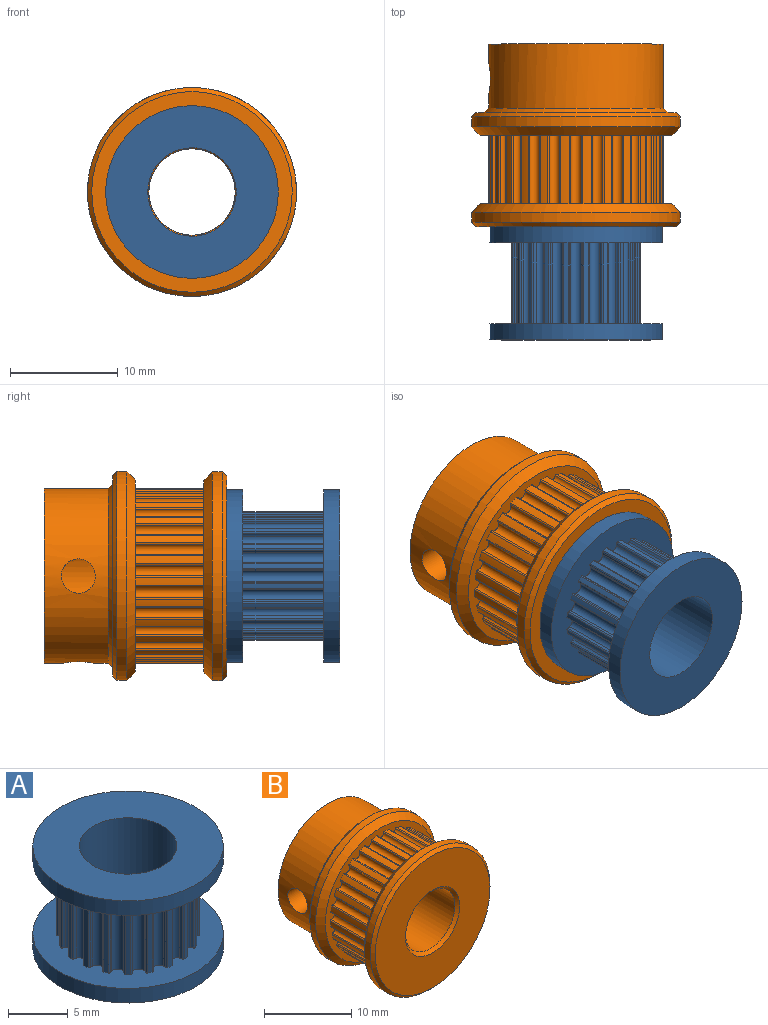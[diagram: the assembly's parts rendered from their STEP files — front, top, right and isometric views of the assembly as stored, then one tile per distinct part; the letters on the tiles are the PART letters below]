
ASSEMBLY  parts=2 mates=1
PART A: 127 faces, bbox 16x16x10.5 mm
  f0: cylinder r=1mm len=7.5mm, axis (0,0,-1), area 1.9mm2, adj f1,f119,f120,f123
  f1: cylinder r=0.15mm len=7.5mm, axis (0,0,-1), area 1.4mm2, adj f0,f2,f120,f123
  f2: cylinder r=6mm len=7.5mm, axis (0,0,-1), area 3.3mm2, adj f1,f3,f120,f123
  f3: cylinder r=0.15mm len=7.5mm, axis (0,0,-1), area 1.4mm2, adj f2,f4,f120,f123
  f4: cylinder r=1mm len=7.5mm, axis (0,0,-1), area 1.9mm2, adj f3,f5,f120,f123
  f5: cylinder r=0.56mm len=7.5mm, axis (0,0,-1), area 9.8mm2, adj f4,f6,f120,f123
  f6: cylinder r=1mm len=7.5mm, axis (0,0,-1), area 1.9mm2, adj f5,f7,f120,f123
  f7: cylinder r=0.15mm len=7.5mm, axis (0,0,-1), area 1.4mm2, adj f6,f8,f120,f123
  f8: cylinder r=6mm len=7.5mm, axis (0,0,-1), area 3.3mm2, adj f7,f9,f120,f123
  f9: cylinder r=0.15mm len=7.5mm, axis (0,0,-1), area 1.4mm2, adj f8,f10,f120,f123
  f10: cylinder r=1mm len=7.5mm, axis (0,0,-1), area 1.9mm2, adj f9,f11,f120,f123
  f11: cylinder r=0.56mm len=7.5mm, axis (0,0,-1), area 9.8mm2, adj f10,f12,f120,f123
  f12: cylinder r=1mm len=7.5mm, axis (0,0,-1), area 1.9mm2, adj f11,f13,f120,f123
  f13: cylinder r=0.15mm len=7.5mm, axis (0,0,-1), area 1.4mm2, adj f12,f14,f120,f123
  f14: cylinder r=6mm len=7.5mm, axis (0,0,-1), area 3.3mm2, adj f13,f15,f120,f123
  f15: cylinder r=0.15mm len=7.5mm, axis (0,0,-1), area 1.4mm2, adj f14,f16,f120,f123
  f16: cylinder r=1mm len=7.5mm, axis (0,0,-1), area 1.9mm2, adj f15,f17,f120,f123
  f17: cylinder r=0.56mm len=7.5mm, axis (0,0,-1), area 9.8mm2, adj f16,f18,f120,f123
  f18: cylinder r=1mm len=7.5mm, axis (0,0,-1), area 1.9mm2, adj f17,f19,f120,f123
  f19: cylinder r=0.15mm len=7.5mm, axis (0,0,-1), area 1.4mm2, adj f18,f20,f120,f123
  f20: cylinder r=6mm len=7.5mm, axis (0,0,-1), area 3.3mm2, adj f19,f21,f120,f123
  f21: cylinder r=0.15mm len=7.5mm, axis (0,0,-1), area 1.4mm2, adj f20,f22,f120,f123
  f22: cylinder r=1mm len=7.5mm, axis (0,0,-1), area 1.9mm2, adj f21,f23,f120,f123
  f23: cylinder r=0.56mm len=7.5mm, axis (0,0,-1), area 9.8mm2, adj f22,f24,f120,f123
  f24: cylinder r=1mm len=7.5mm, axis (0,0,-1), area 1.9mm2, adj f23,f25,f120,f123
  f25: cylinder r=0.15mm len=7.5mm, axis (0,0,-1), area 1.4mm2, adj f24,f26,f120,f123
  f26: cylinder r=6mm len=7.5mm, axis (0,0,-1), area 2.8mm2, adj f25,f27,f120,f123
  f27: cylinder r=0.15mm len=7.5mm, axis (0,0,-1), area 2mm2, adj f26,f28,f120,f123
  f28: cylinder r=1mm len=7.5mm, axis (0,0,-1), area 1.9mm2, adj f27,f29,f120,f123
  f29: cylinder r=0.56mm len=7.5mm, axis (0,0,-1), area 9.8mm2, adj f28,f30,f120,f123
  f30: cylinder r=1mm len=7.5mm, axis (0,0,-1), area 1.9mm2, adj f29,f31,f120,f123
  f31: cylinder r=0.15mm len=7.5mm, axis (0,0,-1), area 1.4mm2, adj f30,f32,f120,f123
  f32: cylinder r=6mm len=7.5mm, axis (0,0,-1), area 3.3mm2, adj f31,f33,f120,f123
  f33: cylinder r=0.15mm len=7.5mm, axis (0,0,-1), area 1.4mm2, adj f32,f34,f120,f123
  f34: cylinder r=1mm len=7.5mm, axis (0,0,-1), area 1.9mm2, adj f33,f35,f120,f123
  f35: cylinder r=0.56mm len=7.5mm, axis (0,0,-1), area 9.8mm2, adj f34,f36,f120,f123
  f36: cylinder r=1mm len=7.5mm, axis (0,0,-1), area 1.9mm2, adj f35,f37,f120,f123
  f37: cylinder r=0.15mm len=7.5mm, axis (0,0,-1), area 1.4mm2, adj f36,f38,f120,f123
  f38: cylinder r=6mm len=7.5mm, axis (0,0,-1), area 3.3mm2, adj f37,f39,f120,f123
  f39: cylinder r=0.15mm len=7.5mm, axis (0,0,-1), area 1.4mm2, adj f38,f40,f120,f123
  f40: cylinder r=1mm len=7.5mm, axis (0,0,-1), area 1.9mm2, adj f39,f41,f120,f123
  f41: cylinder r=0.56mm len=7.5mm, axis (0,0,-1), area 9.8mm2, adj f40,f42,f120,f123
  f42: cylinder r=1mm len=7.5mm, axis (0,0,-1), area 1.9mm2, adj f41,f43,f120,f123
  f43: cylinder r=0.15mm len=7.5mm, axis (0,0,-1), area 1.4mm2, adj f42,f44,f120,f123
  f44: cylinder r=6mm len=7.5mm, axis (0,0,-1), area 3.3mm2, adj f43,f45,f120,f123
  f45: cylinder r=0.15mm len=7.5mm, axis (0,0,-1), area 1.4mm2, adj f44,f46,f120,f123
  f46: cylinder r=1mm len=7.5mm, axis (0,0,-1), area 1.9mm2, adj f45,f47,f120,f123
  f47: cylinder r=0.56mm len=7.5mm, axis (0,0,-1), area 9.8mm2, adj f46,f48,f120,f123
  f48: cylinder r=1mm len=7.5mm, axis (0,0,-1), area 1.9mm2, adj f47,f49,f120,f123
  f49: cylinder r=0.15mm len=7.5mm, axis (0,0,-1), area 1.4mm2, adj f48,f50,f120,f123
  f50: cylinder r=6mm len=7.5mm, axis (0,0,-1), area 3.3mm2, adj f49,f51,f120,f123
  f51: cylinder r=0.15mm len=7.5mm, axis (0,0,-1), area 1.4mm2, adj f50,f52,f120,f123
  f52: cylinder r=1mm len=7.5mm, axis (0,0,-1), area 1.9mm2, adj f51,f53,f120,f123
  f53: cylinder r=0.56mm len=7.5mm, axis (0,0,-1), area 9.8mm2, adj f52,f54,f120,f123
  f54: cylinder r=1mm len=7.5mm, axis (0,0,-1), area 1.9mm2, adj f53,f55,f120,f123
  f55: cylinder r=0.15mm len=7.5mm, axis (0,0,-1), area 1.4mm2, adj f54,f56,f120,f123
  f56: cylinder r=6mm len=7.5mm, axis (0,0,-1), area 3.3mm2, adj f55,f57,f120,f123
  f57: cylinder r=0.15mm len=7.5mm, axis (0,0,-1), area 1.4mm2, adj f56,f58,f120,f123
  f58: cylinder r=1mm len=7.5mm, axis (0,0,-1), area 1.9mm2, adj f57,f59,f120,f123
  f59: cylinder r=0.56mm len=7.5mm, axis (0,0,-1), area 9.8mm2, adj f58,f60,f120,f123
  f60: cylinder r=1mm len=7.5mm, axis (0,0,-1), area 1.9mm2, adj f59,f61,f120,f123
  f61: cylinder r=0.15mm len=7.5mm, axis (0,0,-1), area 1.4mm2, adj f60,f62,f120,f123
  f62: cylinder r=6mm len=7.5mm, axis (0,0,-1), area 3.3mm2, adj f61,f63,f120,f123
  f63: cylinder r=0.15mm len=7.5mm, axis (0,0,-1), area 1.4mm2, adj f62,f64,f120,f123
  f64: cylinder r=1mm len=7.5mm, axis (0,0,-1), area 1.9mm2, adj f63,f65,f120,f123
  f65: cylinder r=0.56mm len=7.5mm, axis (0,0,-1), area 9.8mm2, adj f64,f66,f120,f123
  f66: cylinder r=1mm len=7.5mm, axis (0,0,-1), area 1.9mm2, adj f65,f67,f120,f123
  f67: cylinder r=0.15mm len=7.5mm, axis (0,0,-1), area 1.4mm2, adj f66,f68,f120,f123
  f68: cylinder r=6mm len=7.5mm, axis (0,0,-1), area 3.3mm2, adj f67,f69,f120,f123
  f69: cylinder r=0.15mm len=7.5mm, axis (0,0,-1), area 1.4mm2, adj f68,f70,f120,f123
  f70: cylinder r=1mm len=7.5mm, axis (0,0,-1), area 1.9mm2, adj f69,f71,f120,f123
  f71: cylinder r=0.56mm len=7.5mm, axis (0,0,-1), area 9.8mm2, adj f70,f72,f120,f123
  f72: cylinder r=1mm len=7.5mm, axis (0,0,-1), area 1.9mm2, adj f71,f73,f120,f123
  f73: cylinder r=0.15mm len=7.5mm, axis (0,0,-1), area 1.4mm2, adj f72,f74,f120,f123
  f74: cylinder r=6mm len=7.5mm, axis (0,0,-1), area 3.3mm2, adj f73,f75,f120,f123
  f75: cylinder r=0.15mm len=7.5mm, axis (0,0,-1), area 1.4mm2, adj f74,f76,f120,f123
  f76: cylinder r=1mm len=7.5mm, axis (0,0,-1), area 1.9mm2, adj f75,f77,f120,f123
  f77: cylinder r=0.56mm len=7.5mm, axis (0,0,-1), area 9.8mm2, adj f76,f78,f120,f123
  f78: cylinder r=1mm len=7.5mm, axis (0,0,-1), area 1.9mm2, adj f77,f79,f120,f123
  f79: cylinder r=0.15mm len=7.5mm, axis (0,0,-1), area 1.4mm2, adj f78,f80,f120,f123
  f80: cylinder r=6mm len=7.5mm, axis (0,0,-1), area 3.3mm2, adj f79,f81,f120,f123
  f81: cylinder r=0.15mm len=7.5mm, axis (0,0,-1), area 1.4mm2, adj f80,f82,f120,f123
  f82: cylinder r=1mm len=7.5mm, axis (0,0,-1), area 1.9mm2, adj f81,f83,f120,f123
  f83: cylinder r=0.56mm len=7.5mm, axis (0,0,-1), area 9.8mm2, adj f82,f84,f120,f123
  f84: cylinder r=1mm len=7.5mm, axis (0,0,-1), area 1.9mm2, adj f83,f85,f120,f123
  f85: cylinder r=0.15mm len=7.5mm, axis (0,0,-1), area 1.4mm2, adj f84,f86,f120,f123
  f86: cylinder r=6mm len=7.5mm, axis (0,0,-1), area 3.3mm2, adj f85,f87,f120,f123
  f87: cylinder r=0.15mm len=7.5mm, axis (0,0,-1), area 1.4mm2, adj f86,f88,f120,f123
  f88: cylinder r=1mm len=7.5mm, axis (0,0,-1), area 1.9mm2, adj f87,f89,f120,f123
  f89: cylinder r=0.56mm len=7.5mm, axis (0,0,-1), area 9.8mm2, adj f88,f90,f120,f123
  f90: cylinder r=1mm len=7.5mm, axis (0,0,-1), area 1.9mm2, adj f89,f91,f120,f123
  f91: cylinder r=0.15mm len=7.5mm, axis (0,0,-1), area 1.4mm2, adj f90,f92,f120,f123
  f92: cylinder r=6mm len=7.5mm, axis (0,0,-1), area 3.3mm2, adj f91,f93,f120,f123
  f93: cylinder r=0.15mm len=7.5mm, axis (0,0,-1), area 1.4mm2, adj f92,f94,f120,f123
  f94: cylinder r=1mm len=7.5mm, axis (0,0,-1), area 1.9mm2, adj f93,f95,f120,f123
  f95: cylinder r=0.56mm len=7.5mm, axis (0,0,-1), area 9.8mm2, adj f94,f96,f120,f123
  f96: cylinder r=1mm len=7.5mm, axis (0,0,-1), area 1.9mm2, adj f95,f97,f120,f123
  f97: cylinder r=0.15mm len=7.5mm, axis (0,0,-1), area 1.4mm2, adj f96,f98,f120,f123
  f98: cylinder r=6mm len=7.5mm, axis (0,0,-1), area 3.3mm2, adj f97,f99,f120,f123
  f99: cylinder r=0.15mm len=7.5mm, axis (0,0,-1), area 1.4mm2, adj f98,f100,f120,f123
  f100: cylinder r=1mm len=7.5mm, axis (0,0,-1), area 1.9mm2, adj f99,f101,f120,f123
  f101: cylinder r=0.56mm len=7.5mm, axis (0,0,-1), area 9.8mm2, adj f100,f102,f120,f123
  f102: cylinder r=1mm len=7.5mm, axis (0,0,-1), area 1.9mm2, adj f101,f103,f120,f123
  f103: cylinder r=0.15mm len=7.5mm, axis (0,0,-1), area 1.4mm2, adj f102,f104,f120,f123
  f104: cylinder r=6mm len=7.5mm, axis (0,0,-1), area 3.3mm2, adj f103,f105,f120,f123
  f105: cylinder r=0.15mm len=7.5mm, axis (0,0,-1), area 1.4mm2, adj f104,f106,f120,f123
  f106: cylinder r=1mm len=7.5mm, axis (0,0,-1), area 1.9mm2, adj f105,f107,f120,f123
  f107: cylinder r=0.56mm len=7.5mm, axis (0,0,-1), area 9.8mm2, adj f106,f108,f120,f123
  f108: cylinder r=1mm len=7.5mm, axis (0,0,-1), area 1.9mm2, adj f107,f109,f120,f123
  f109: cylinder r=0.15mm len=7.5mm, axis (0,0,-1), area 1.4mm2, adj f108,f110,f120,f123
  f110: cylinder r=6mm len=7.5mm, axis (0,0,-1), area 3.3mm2, adj f109,f111,f120,f123
  f111: cylinder r=0.15mm len=7.5mm, axis (0,0,-1), area 1.4mm2, adj f110,f112,f120,f123
  f112: cylinder r=1mm len=7.5mm, axis (0,0,-1), area 1.9mm2, adj f111,f113,f120,f123
  f113: cylinder r=0.56mm len=7.5mm, axis (0,0,-1), area 9.8mm2, adj f112,f114,f120,f123
  f114: cylinder r=1mm len=7.5mm, axis (0,0,-1), area 1.9mm2, adj f113,f115,f120,f123
  f115: cylinder r=0.15mm len=7.5mm, axis (0,0,-1), area 1.4mm2, adj f114,f116,f120,f123
  f116: cylinder r=6mm len=7.5mm, axis (0,0,-1), area 3.3mm2, adj f115,f117,f120,f123
  f117: cylinder r=0.15mm len=7.5mm, axis (0,0,-1), area 1.4mm2, adj f116,f118,f120,f123
  f118: cylinder r=1mm len=7.5mm, axis (0,0,-1), area 1.9mm2, adj f117,f119,f120,f123
  f119: cylinder r=0.56mm len=7.5mm, axis (0,0,-1), area 9.8mm2, adj f0,f118,f120,f123
  f120: plane 16x16mm, normal (0,0,-1), area 102.3mm2, adj f0,f1,f2,f3,f4,f5,f6,f7
  f121: cylinder r=8mm len=16mm, axis (0,0,-1), area 75.4mm2, adj f120,f122
  f122: plane 16x16mm, normal (0,0,1), area 148.3mm2, adj f121,f126
  f123: plane 16x16mm, normal (0,0,1), area 102.3mm2, adj f0,f1,f2,f3,f4,f5,f6,f7
  f124: cylinder r=8mm len=16mm, axis (0,0,1), area 75.4mm2, adj f123,f125
  f125: plane 16x16mm, normal (0,0,-1), area 148.3mm2, adj f124,f126
  f126: cylinder r=4.1mm len=10.5mm, axis (0,0,-1), area 270.5mm2, adj f122,f125
PART B: 117 faces, bbox 19.4x16.9x19.4 mm
  f0: cylinder r=8.1mm len=16.21mm, axis (0,-1,0), area 287.2mm2, adj f1,f108,f114,f116
  f1: cylinder r=1.59mm len=4.43mm, axis (1,0,0), area 41.8mm2, adj f0,f109
  f2: cylinder r=0.5mm len=6.35mm, axis (0,1,0), area 9.8mm2, adj f3,f101,f102,f105
  f3: cylinder r=0.12mm len=6.35mm, axis (0,1,0), area 1.3mm2, adj f2,f4,f102,f105
  f4: cylinder r=8.1mm len=6.35mm, axis (0,1,0), area 4.9mm2, adj f3,f5,f102,f105
  f5: cylinder r=0.12mm len=6.35mm, axis (0,1,0), area 1.3mm2, adj f4,f6,f102,f105
  f6: cylinder r=0.5mm len=6.35mm, axis (0,1,0), area 9.8mm2, adj f5,f7,f102,f105
  f7: cylinder r=0.12mm len=6.35mm, axis (0,1,0), area 1.3mm2, adj f6,f8,f102,f105
  f8: cylinder r=8.1mm len=6.35mm, axis (0,1,0), area 4.9mm2, adj f7,f9,f102,f105
  f9: cylinder r=0.12mm len=6.35mm, axis (0,1,0), area 1.3mm2, adj f8,f10,f102,f105
  f10: cylinder r=0.5mm len=6.35mm, axis (0,1,0), area 9.8mm2, adj f9,f11,f102,f105
  f11: cylinder r=0.12mm len=6.35mm, axis (0,1,0), area 1.3mm2, adj f10,f12,f102,f105
  f12: cylinder r=8.1mm len=6.35mm, axis (0,1,0), area 4.9mm2, adj f11,f13,f102,f105
  f13: cylinder r=0.12mm len=6.35mm, axis (0,1,0), area 1.3mm2, adj f12,f14,f102,f105
  f14: cylinder r=0.5mm len=6.35mm, axis (0,1,0), area 9.8mm2, adj f13,f15,f102,f105
  f15: cylinder r=0.12mm len=6.35mm, axis (0,1,0), area 1.3mm2, adj f14,f16,f102,f105
  f16: cylinder r=8.1mm len=6.35mm, axis (0,1,0), area 4.9mm2, adj f15,f17,f102,f105
  f17: cylinder r=0.12mm len=6.35mm, axis (0,1,0), area 1.3mm2, adj f16,f18,f102,f105
  f18: cylinder r=0.5mm len=6.35mm, axis (0,1,0), area 9.8mm2, adj f17,f19,f102,f105
  f19: cylinder r=0.12mm len=6.35mm, axis (0,1,0), area 1.3mm2, adj f18,f20,f102,f105
  f20: cylinder r=8.1mm len=6.35mm, axis (0,1,0), area 4.9mm2, adj f19,f21,f102,f105
  f21: cylinder r=0.12mm len=6.35mm, axis (0,1,0), area 1.3mm2, adj f20,f22,f102,f105
  f22: cylinder r=0.5mm len=6.35mm, axis (0,1,0), area 9.8mm2, adj f21,f23,f102,f105
  f23: cylinder r=0.12mm len=6.35mm, axis (0,1,0), area 1.3mm2, adj f22,f24,f102,f105
  f24: cylinder r=8.1mm len=6.35mm, axis (0,1,0), area 4.9mm2, adj f23,f25,f102,f105
  f25: cylinder r=0.12mm len=6.35mm, axis (0,1,0), area 1.3mm2, adj f24,f26,f102,f105
  f26: cylinder r=0.5mm len=6.35mm, axis (0,1,0), area 9.8mm2, adj f25,f27,f102,f105
  f27: cylinder r=0.12mm len=6.35mm, axis (0,1,0), area 1.3mm2, adj f26,f28,f102,f105
  f28: cylinder r=8.1mm len=6.35mm, axis (0,1,0), area 4.9mm2, adj f27,f29,f102,f105
  f29: cylinder r=0.12mm len=6.35mm, axis (0,1,0), area 1.3mm2, adj f28,f30,f102,f105
  f30: cylinder r=0.5mm len=6.35mm, axis (0,1,0), area 9.8mm2, adj f29,f31,f102,f105
  f31: cylinder r=0.12mm len=6.35mm, axis (0,1,0), area 1.3mm2, adj f30,f32,f102,f105
  f32: cylinder r=8.1mm len=6.35mm, axis (0,1,0), area 4.9mm2, adj f31,f33,f102,f105
  f33: cylinder r=0.12mm len=6.35mm, axis (0,1,0), area 1.3mm2, adj f32,f34,f102,f105
  f34: cylinder r=0.5mm len=6.35mm, axis (0,1,0), area 9.8mm2, adj f33,f35,f102,f105
  f35: cylinder r=0.12mm len=6.35mm, axis (0,1,0), area 1.3mm2, adj f34,f36,f102,f105
  f36: cylinder r=8.1mm len=6.35mm, axis (0,1,0), area 4.9mm2, adj f35,f37,f102,f105
  f37: cylinder r=0.12mm len=6.35mm, axis (0,1,0), area 1.3mm2, adj f36,f38,f102,f105
  f38: cylinder r=0.5mm len=6.35mm, axis (0,1,0), area 9.8mm2, adj f37,f39,f102,f105
  f39: cylinder r=0.12mm len=6.35mm, axis (0,1,0), area 1.3mm2, adj f38,f40,f102,f105
  f40: cylinder r=8.1mm len=6.35mm, axis (0,1,0), area 4.9mm2, adj f39,f41,f102,f105
  f41: cylinder r=0.12mm len=6.35mm, axis (0,1,0), area 1.3mm2, adj f40,f42,f102,f105
  f42: cylinder r=0.5mm len=6.35mm, axis (0,1,0), area 9.8mm2, adj f41,f43,f102,f105
  f43: cylinder r=0.12mm len=6.35mm, axis (0,1,0), area 1.3mm2, adj f42,f44,f102,f105
  f44: cylinder r=8.1mm len=6.35mm, axis (0,1,0), area 4.9mm2, adj f43,f45,f102,f105
  f45: cylinder r=0.12mm len=6.35mm, axis (0,1,0), area 1.3mm2, adj f44,f46,f102,f105
  f46: cylinder r=0.5mm len=6.35mm, axis (0,1,0), area 9.8mm2, adj f45,f47,f102,f105
  f47: cylinder r=0.12mm len=6.35mm, axis (0,1,0), area 1.3mm2, adj f46,f48,f102,f105
  f48: cylinder r=8.1mm len=6.35mm, axis (0,1,0), area 4.9mm2, adj f47,f49,f102,f105
  f49: cylinder r=0.12mm len=6.35mm, axis (0,1,0), area 1.3mm2, adj f48,f50,f102,f105
  f50: cylinder r=0.5mm len=6.35mm, axis (0,1,0), area 9.8mm2, adj f49,f51,f102,f105
  f51: cylinder r=0.12mm len=6.35mm, axis (0,1,0), area 1.3mm2, adj f50,f52,f102,f105
  f52: cylinder r=8.1mm len=6.35mm, axis (0,1,0), area 4.9mm2, adj f51,f53,f102,f105
  f53: cylinder r=0.12mm len=6.35mm, axis (0,1,0), area 1.3mm2, adj f52,f54,f102,f105
  f54: cylinder r=0.5mm len=6.35mm, axis (0,1,0), area 9.8mm2, adj f53,f55,f102,f105
  f55: cylinder r=0.12mm len=6.35mm, axis (0,1,0), area 1.3mm2, adj f54,f56,f102,f105
  f56: cylinder r=8.1mm len=6.35mm, axis (0,1,0), area 4.9mm2, adj f55,f57,f102,f105
  f57: cylinder r=0.12mm len=6.35mm, axis (0,1,0), area 1.3mm2, adj f56,f58,f102,f105
  f58: cylinder r=0.5mm len=6.35mm, axis (0,1,0), area 9.8mm2, adj f57,f59,f102,f105
  f59: cylinder r=0.12mm len=6.35mm, axis (0,1,0), area 1.3mm2, adj f58,f60,f102,f105
  f60: cylinder r=8.1mm len=6.35mm, axis (0,1,0), area 4.9mm2, adj f59,f61,f102,f105
  f61: cylinder r=0.12mm len=6.35mm, axis (0,1,0), area 1.3mm2, adj f60,f62,f102,f105
  f62: cylinder r=0.5mm len=6.35mm, axis (0,1,0), area 9.8mm2, adj f61,f63,f102,f105
  f63: cylinder r=0.12mm len=6.35mm, axis (0,1,0), area 1.3mm2, adj f62,f64,f102,f105
  f64: cylinder r=8.1mm len=6.35mm, axis (0,1,0), area 4.9mm2, adj f63,f65,f102,f105
  f65: cylinder r=0.12mm len=6.35mm, axis (0,1,0), area 1.3mm2, adj f64,f66,f102,f105
  f66: cylinder r=0.5mm len=6.35mm, axis (0,1,0), area 9.8mm2, adj f65,f67,f102,f105
  f67: cylinder r=0.12mm len=6.35mm, axis (0,1,0), area 1.3mm2, adj f66,f68,f102,f105
  f68: cylinder r=8.1mm len=6.35mm, axis (0,1,0), area 4.9mm2, adj f67,f69,f102,f105
  f69: cylinder r=0.12mm len=6.35mm, axis (0,1,0), area 1.3mm2, adj f68,f70,f102,f105
  f70: cylinder r=0.5mm len=6.35mm, axis (0,1,0), area 9.8mm2, adj f69,f71,f102,f105
  f71: cylinder r=0.12mm len=6.35mm, axis (0,1,0), area 1.3mm2, adj f70,f72,f102,f105
  f72: cylinder r=8.1mm len=6.35mm, axis (0,1,0), area 4.9mm2, adj f71,f73,f102,f105
  f73: cylinder r=0.12mm len=6.35mm, axis (0,1,0), area 1.3mm2, adj f72,f74,f102,f105
  f74: cylinder r=0.5mm len=6.35mm, axis (0,1,0), area 9.8mm2, adj f73,f75,f102,f105
  f75: cylinder r=0.12mm len=6.35mm, axis (0,1,0), area 1.3mm2, adj f74,f76,f102,f105
  f76: cylinder r=8.1mm len=6.35mm, axis (0,1,0), area 4.9mm2, adj f75,f77,f102,f105
  f77: cylinder r=0.12mm len=6.35mm, axis (0,1,0), area 1.3mm2, adj f76,f78,f102,f105
  f78: cylinder r=0.5mm len=6.35mm, axis (0,1,0), area 9.8mm2, adj f77,f79,f102,f105
  f79: cylinder r=0.12mm len=6.35mm, axis (0,1,0), area 1.3mm2, adj f78,f80,f102,f105
  f80: cylinder r=8.1mm len=6.35mm, axis (0,1,0), area 4.9mm2, adj f79,f81,f102,f105
  f81: cylinder r=0.12mm len=6.35mm, axis (0,1,0), area 1.3mm2, adj f80,f82,f102,f105
  f82: cylinder r=0.5mm len=6.35mm, axis (0,1,0), area 9.8mm2, adj f81,f83,f102,f105
  f83: cylinder r=0.12mm len=6.35mm, axis (0,1,0), area 1.3mm2, adj f82,f84,f102,f105
  f84: cylinder r=8.1mm len=6.35mm, axis (0,1,0), area 4.9mm2, adj f83,f85,f102,f105
  f85: cylinder r=0.12mm len=6.35mm, axis (0,1,0), area 1.3mm2, adj f84,f86,f102,f105
  f86: cylinder r=0.5mm len=6.35mm, axis (0,1,0), area 9.8mm2, adj f85,f87,f102,f105
  f87: cylinder r=0.12mm len=6.35mm, axis (0,1,0), area 1.3mm2, adj f86,f88,f102,f105
  f88: cylinder r=8.1mm len=6.35mm, axis (0,1,0), area 4.9mm2, adj f87,f89,f102,f105
  f89: cylinder r=0.12mm len=6.35mm, axis (0,1,0), area 1.3mm2, adj f88,f90,f102,f105
  f90: cylinder r=0.5mm len=6.35mm, axis (0,1,0), area 9.8mm2, adj f89,f91,f102,f105
  f91: cylinder r=0.12mm len=6.35mm, axis (0,1,0), area 1.3mm2, adj f90,f92,f102,f105
  f92: cylinder r=8.1mm len=6.35mm, axis (0,1,0), area 4.9mm2, adj f91,f93,f102,f105
  f93: cylinder r=0.12mm len=6.35mm, axis (0,1,0), area 1.3mm2, adj f92,f94,f102,f105
  f94: cylinder r=0.5mm len=6.35mm, axis (0,1,0), area 9.8mm2, adj f93,f95,f102,f105
  f95: cylinder r=0.12mm len=6.35mm, axis (0,1,0), area 1.3mm2, adj f94,f96,f102,f105
  f96: cylinder r=8.1mm len=6.35mm, axis (0,1,0), area 4.9mm2, adj f95,f97,f102,f105
  f97: cylinder r=0.12mm len=6.35mm, axis (0,1,0), area 1.3mm2, adj f96,f98,f102,f105
  f98: cylinder r=0.5mm len=6.35mm, axis (0,1,0), area 9.8mm2, adj f97,f99,f102,f105
  f99: cylinder r=0.12mm len=6.35mm, axis (0,1,0), area 1.3mm2, adj f98,f100,f102,f105
  f100: cylinder r=8.1mm len=6.35mm, axis (0,1,0), area 4.9mm2, adj f99,f101,f102,f105
  f101: cylinder r=0.12mm len=6.35mm, axis (0,1,0), area 1.3mm2, adj f2,f100,f102,f105
  f102: plane 17.8x17.8mm, normal (0,-1,0), area 55.4mm2, adj f2,f3,f4,f5,f6,f7,f8,f9
  f103: cylinder r=9.69mm len=19.38mm, axis (0,-1,0), area 56.4mm2, adj f110,f115
  f104: plane 18.59x18.59mm, normal (0,1,0), area 44.4mm2, adj f114,f115
  f105: plane 17.8x17.8mm, normal (0,1,0), area 55.4mm2, adj f2,f3,f4,f5,f6,f7,f8,f9
  f106: cylinder r=9.69mm len=19.38mm, axis (0,1,0), area 56.4mm2, adj f111,f113
  f107: plane 18.59x18.59mm, normal (0,-1,0), area 210.7mm2, adj f112,f113
  f108: plane 16.21x16.21mm, normal (0,1,0), area 156mm2, adj f0,f109
  f109: cylinder r=4mm len=16.54mm, axis (0,1,0), area 399.4mm2, adj f1,f108,f112,f116
  f110: cone r=9.69mm half-angle=45deg, axis (0,1,0), area 65.6mm2, adj f102,f103
  f111: cone r=9.69mm half-angle=45deg, axis (0,-1,0), area 65.6mm2, adj f105,f106
  f112: cone r=4.4mm half-angle=45deg, axis (0,-1,0), area 14.8mm2, adj f107,f109
  f113: cone r=9.29mm half-angle=45deg, axis (0,1,0), area 33.5mm2, adj f106,f107
  f114: cone r=8.1mm half-angle=45deg, axis (0,-1,0), area 29.3mm2, adj f0,f104
  f115: cone r=9.29mm half-angle=45deg, axis (0,-1,0), area 33.5mm2, adj f103,f104
  f116: cylinder r=1.59mm len=4.43mm, axis (0,0,1), area 41.8mm2, adj f0,f109
PLACE A rot(axis=(1,0,0),90deg) t=(-15.23,-25.54,4.22)mm
PLACE B t=(-15.23,-15.57,4.22)mm
MATE parallel A.f2 <-> B.f0  axis (0,1,0) through (-15.23,-24.04,4.22)mm
